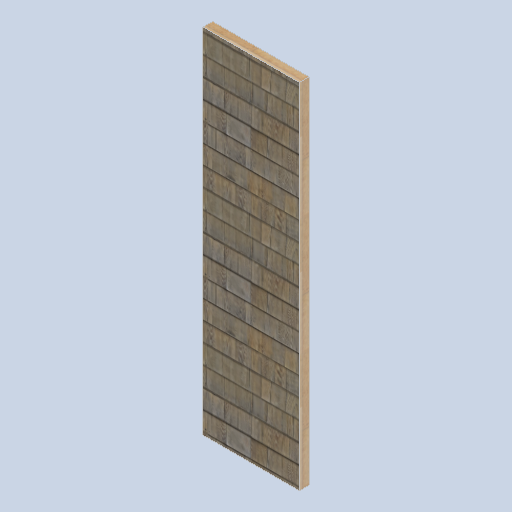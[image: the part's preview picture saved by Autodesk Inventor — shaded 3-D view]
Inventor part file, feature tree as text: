
AUTODESK INVENTOR PART (.ipt)
format: ipt  version: 2024.2 (Build 282272000, 272)  size: 186,368 bytes
history: native  units: in
note: dims shown in document units (in); Inventor stores cm internally (conversion verified against a paired STEP export)
features: other x3, sketch x1
ambient origin geometry x8: Origin, YZ Plane, XZ Plane, XY Plane, X Axis, Y Axis, Z Axis, Center Point
bodies: Solid1 (feature_tree)
feature tree (4):
  other  "front_wall_block04_MIR.ipt"
  other  "Solid1::front_wall_block04_MIR.ipt"
  other  "TaggingFeature1"
  sketch  "Sketch1"  dims[d0=0.3937in]
